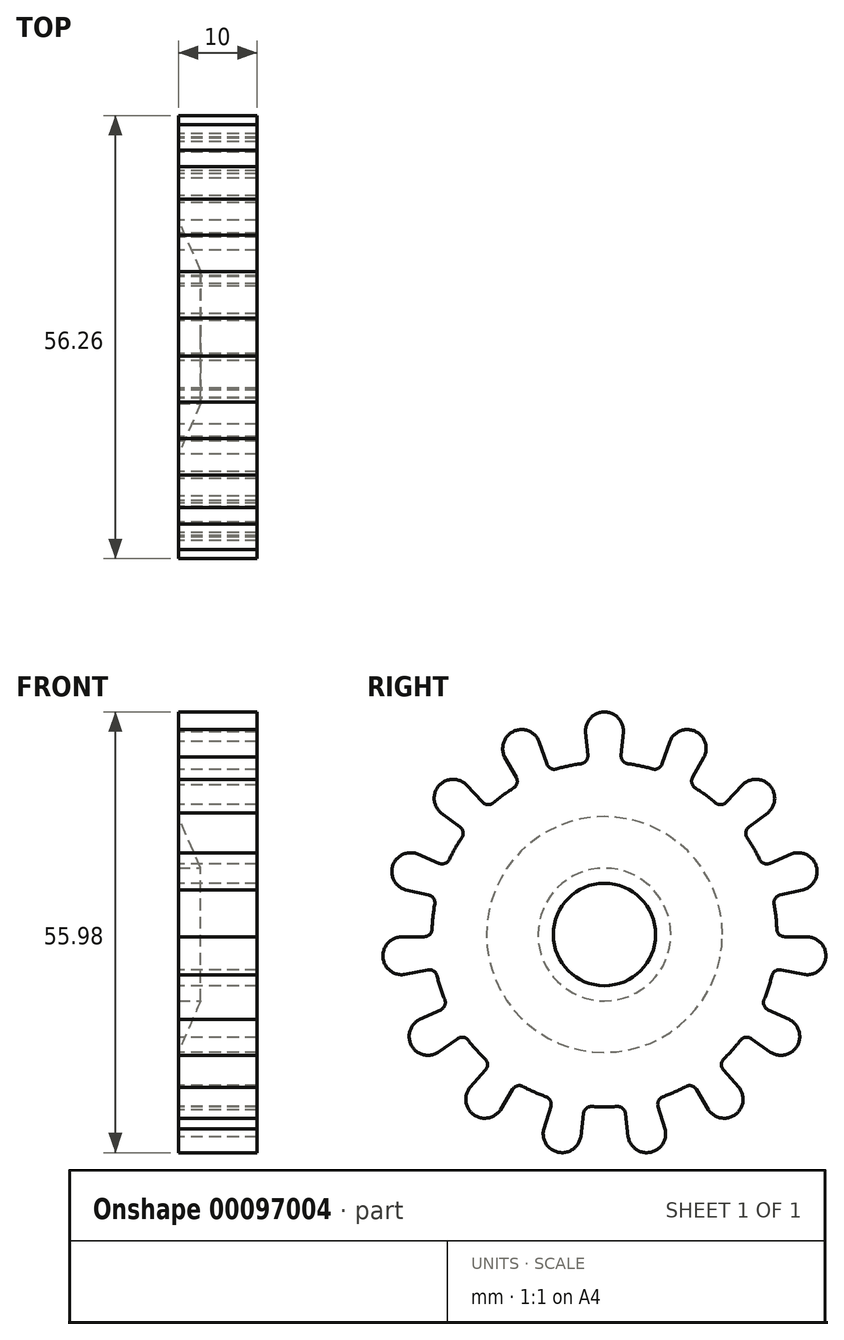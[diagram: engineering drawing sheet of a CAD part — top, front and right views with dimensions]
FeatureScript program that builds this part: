
annotation { "Feature Type Name" : "Feature", "Feature Type Description" : "" }
export const myFeature = defineFeature(function(context is Context, id is Id, definition is map)
    precondition{}
    {
        {
            var Q0;
            Q0=qCreatedBy(makeId("Right.planeOp"),FACE);
            var sketch = newSketch(context, id + "F0", { "sketchPlane" : qUnion([Q0])});
            skCircle(sketch, "E0", {"center": v(0, 0) * mm, "radius": 6.5 * mm});
            skCircle(sketch, "E1", {"center": v(0, 0) * mm, "radius": 21.9 * mm});
            skArc(sketch, "E2", {"start": v(2.38, 25.54) * mm, "mid": v(0, 28.28) * mm, "end": v(-2.38, 25.54) * mm});
            skLineSegment(sketch, "E3", {"start": v(-2.4, 25.76) * mm, "end": v(-2.03, 21.8) * mm});
            skLineSegment(sketch, "E4", {"start": v(2.4, 25.76) * mm, "end": v(2.03, 21.8) * mm});
            skSolve(sketch);
        }
        {
            var Q0;
            Q0=makeQuery(id+"F0.imprint","IMPRINT",FACE,{"disambiguationData":[TD([[makeQuery(id+"F0.imprint","IMPRINT",EDGE,{"derivedFrom":sQuery(id+"F0.wireOp",EDGE,"E0")}),-1.0]])]});
            var Q1;
            {var subQ0=sQuery(id+"F0.wireOp",EDGE,"E3");var subQ3=sQuery(id+"F0.wireOp",EDGE,"E1");var subQ4=makeQuery(id+"F0.imprint","INTERSECT",VERTEX,{"derivedFrom":[subQ3,subQ0]});Q1=makeQuery(id+"F0.imprint","IMPRINT",FACE,{"disambiguationData":[TD([[makeQuery(id+"F0.imprint","IMPRINT",EDGE,{"disambiguationData":[TD([[subQ4,1.0]])],"derivedFrom":subQ3}),-1.0]])]});}
            extrude(context, id + "F1", {"entities" : qUnion([Q0, Q1]), "endBound" : BoundingType.SYMMETRIC, "depth" : 10 * mm});
        }
        {
            var Q0;
            Q0=makeQuery(id+"F1.opExtrude","SWEPT_EDGE",EDGE,{"disambiguationData":[OSD([sQuery(id+"F0.wireOp",EDGE,"E1"),sQuery(id+"F0.wireOp",EDGE,"E3")])]});
            fillet(context, id + "F2", {"entities" : qUnion([Q0]), "radius" : 1 * mm, "tangentPropagation" : true, "allowEdgeOverflow" : false});
        }
        {
            var Q0;
            Q0=makeQuery(id+"F1.opExtrude","SWEPT_EDGE",EDGE,{"disambiguationData":[OSD([sQuery(id+"F0.wireOp",EDGE,"E1"),sQuery(id+"F0.wireOp",EDGE,"E4")])]});
            fillet(context, id + "F3", {"entities" : qUnion([Q0]), "radius" : 1 * mm, "tangentPropagation" : true, "allowEdgeOverflow" : false});
        }
        {
            var Q0;
            Q0=makeQuery(id+"F1.opExtrude","SWEPT_FACE",FACE,{"disambiguationData":[OSD([sQuery(id+"F0.wireOp",EDGE,"E3")])]});
            var Q1;
            Q1=makeQuery(id+"F1.opExtrude","SWEPT_FACE",FACE,{"disambiguationData":[OSD([sQuery(id+"F0.wireOp",EDGE,"E2")])]});
            var Q2;
            Q2=makeQuery(id+"F2.opFillet","BLEND_FACE",FACE,{"disambiguationData":[OSD([sQuery(id+"F0.wireOp",EDGE,"E1"),sQuery(id+"F0.wireOp",EDGE,"E3")])]});
            var Q3;
            Q3=makeQuery(id+"F1.opExtrude","SWEPT_FACE",FACE,{"disambiguationData":[OSD([sQuery(id+"F0.wireOp",EDGE,"E4")])]});
            var Q4;
            Q4=makeQuery(id+"F3.opFillet","BLEND_FACE",FACE,{"disambiguationData":[OSD([sQuery(id+"F0.wireOp",EDGE,"E1"),sQuery(id+"F0.wireOp",EDGE,"E4")])]});
            var Q5;
            Q5=makeQuery(id+"F1.opExtrude","CAP_EDGE",EDGE,{"disambiguationData":[OSD([sQuery(id+"F0.wireOp",EDGE,"E0")])],"isStart":false});
            circularPattern(context, id + "F5", {"patternType" : PatternType.FACE, "faces" : qUnion([Q0, Q1, Q2, Q3, Q4]), "axis" : qUnion([Q5]), "angle" : 24 * degree, "instanceCount" : 15});
        }
        {
            var Q0;
            Q0=qCreatedBy(makeId("Front.planeOp"),FACE);
            var sketch = newSketch(context, id + "F6", { "sketchPlane" : qUnion([Q0])});
            skLineSegment(sketch, "E5", {"start": v(0, 0) * mm, "end": v(0, 8.43) * mm});
            skLineSegment(sketch, "E6", {"start": v(0, 8.43) * mm, "end": v(0, 8.43) * mm});
            skLineSegment(sketch, "E7", {"start": v(-2.18, 8.43) * mm, "end": v(-5.07, 15.15) * mm});
            skLineSegment(sketch, "E8", {"start": v(-5.07, 15.15) * mm, "end": v(-5.14, 8.43) * mm});
            skLineSegment(sketch, "E9", {"start": v(-5.14, 8.43) * mm, "end": v(-2.18, 8.43) * mm});
            skSolve(sketch);
        }
        {
            var Q0;
            Q0=qSketchRegion(id+"F6",true);
            var Q1;
            Q1=makeQuery(id+"F1.opExtrude","SWEPT_FACE",FACE,{"disambiguationData":[OSD([sQuery(id+"F0.wireOp",EDGE,"E0")])]});
            revolve(context, id + "F7", {"operationType" : NewBodyOperationType.REMOVE, "entities" : qUnion([Q0]), "axis" : qUnion([Q1]), "revolveType" : RevolveType.FULL, "oppositeDirection" : true});
        }
    });
